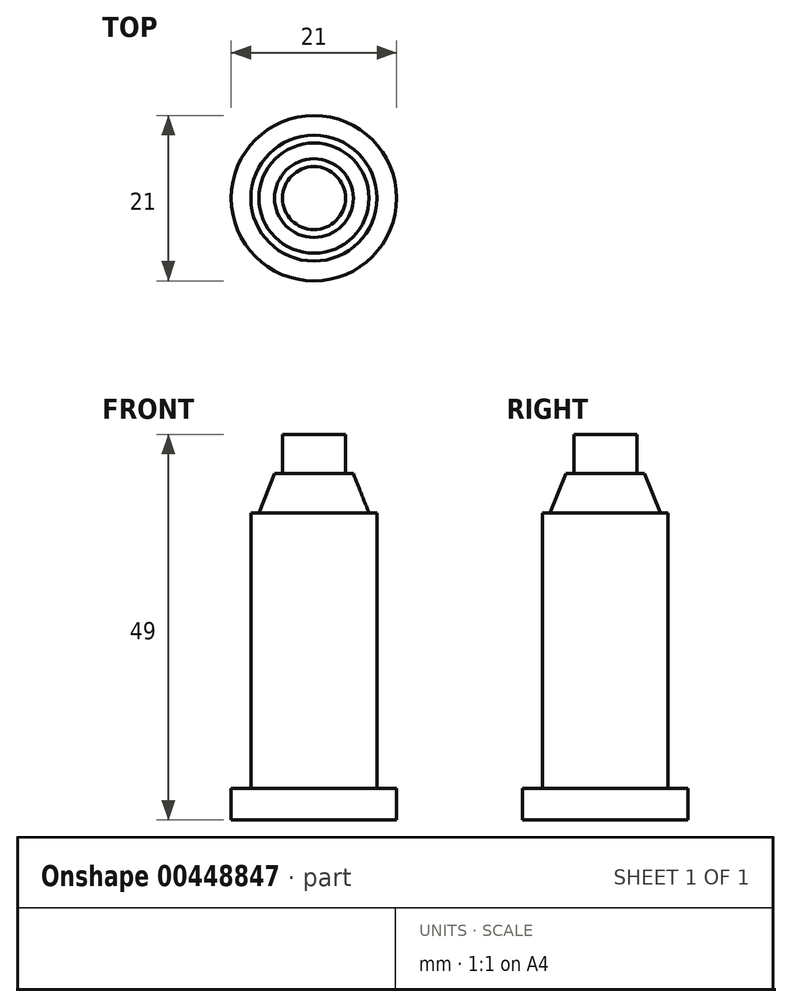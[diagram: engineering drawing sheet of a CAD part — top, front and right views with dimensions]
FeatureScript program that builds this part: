
annotation { "Feature Type Name" : "Feature", "Feature Type Description" : "" }
export const myFeature = defineFeature(function(context is Context, id is Id, definition is map)
    precondition{}
    {
        {
            var Q0;
            Q0=qCreatedBy(makeId("Top.planeOp"),FACE);
            var sketch = newSketch(context, id + "F0", { "sketchPlane" : qUnion([Q0])});
            skCircle(sketch, "E0", {"center": v(0, 0) * mm, "radius": 10.5 * mm});
            skSolve(sketch);
        }
        {
            var Q0;
            Q0=qSketchRegion(id+"F0",true);
            extrude(context, id + "F1", {"entities" : qUnion([Q0]), "depth" : 4 * mm});
        }
        {
            var Q0;
            Q0=qCreatedBy(makeId("Top.planeOp"),FACE);
            var sketch = newSketch(context, id + "F2", { "sketchPlane" : qUnion([Q0])});
            skCircle(sketch, "E1", {"center": v(0, 0) * mm, "radius": 8 * mm});
            skSolve(sketch);
        }
        {
            var Q0;
            Q0=qSketchRegion(id+"F2",true);
            extrude(context, id + "F3", {"entities" : qUnion([Q0]), "operationType" : NewBodyOperationType.ADD, "depth" : 39 * mm});
        }
        {
            var Q0;
            Q0=qCreatedBy(makeId("Right.planeOp"),FACE);
            var sketch = newSketch(context, id + "F4", { "sketchPlane" : qUnion([Q0])});
            skLineSegment(sketch, "E2", {"start": v(0, 44) * mm, "end": v(0, 39) * mm});
            skLineSegment(sketch, "E3", {"start": v(0, 39) * mm, "end": v(7, 39) * mm});
            skLineSegment(sketch, "E4", {"start": v(7, 39) * mm, "end": v(5, 44) * mm});
            skLineSegment(sketch, "E5", {"start": v(5, 44) * mm, "end": v(0, 44) * mm});
            skSolve(sketch);
        }
        {
            var Q0;
            Q0=makeQuery(id+"F4.imprint","IMPRINT",FACE,{"disambiguationData":[TD([[makeQuery(id+"F4.imprint","IMPRINT",EDGE,{"derivedFrom":sQuery(id+"F4.wireOp",EDGE,"E2")}),1.0]])]});
            var Q1;
            Q1=sQuery(id+"F4.wireOp",EDGE,"E2");
            revolve(context, id + "F5", {"operationType" : NewBodyOperationType.ADD, "entities" : qUnion([Q0]), "axis" : qUnion([Q1]), "revolveType" : RevolveType.FULL});
        }
        {
            var Q0;
            Q0=qCreatedBy(makeId("Right.planeOp"),FACE);
            var sketch = newSketch(context, id + "F6", { "sketchPlane" : qUnion([Q0])});
            skLineSegment(sketch, "E6.bottom", {"start": v(0, 49) * mm, "end": v(4, 49) * mm});
            skLineSegment(sketch, "E6.top", {"start": v(0, 44) * mm, "end": v(4, 44) * mm});
            skLineSegment(sketch, "E6.left", {"start": v(0, 49) * mm, "end": v(0, 44) * mm});
            skLineSegment(sketch, "E6.right", {"start": v(4, 49) * mm, "end": v(4, 44) * mm});
            skSolve(sketch);
        }
        {
            var Q0;
            Q0=makeQuery(id+"F6.imprint","IMPRINT",FACE,{"disambiguationData":[TD([[makeQuery(id+"F6.imprint","IMPRINT",EDGE,{"derivedFrom":sQuery(id+"F6.wireOp",EDGE,"E6.bottom")}),-1.0]])]});
            var Q1;
            Q1=sQuery(id+"F6.wireOp",EDGE,"E6.left");
            revolve(context, id + "F7", {"operationType" : NewBodyOperationType.ADD, "entities" : qUnion([Q0]), "axis" : qUnion([Q1]), "revolveType" : RevolveType.FULL});
        }
    });
